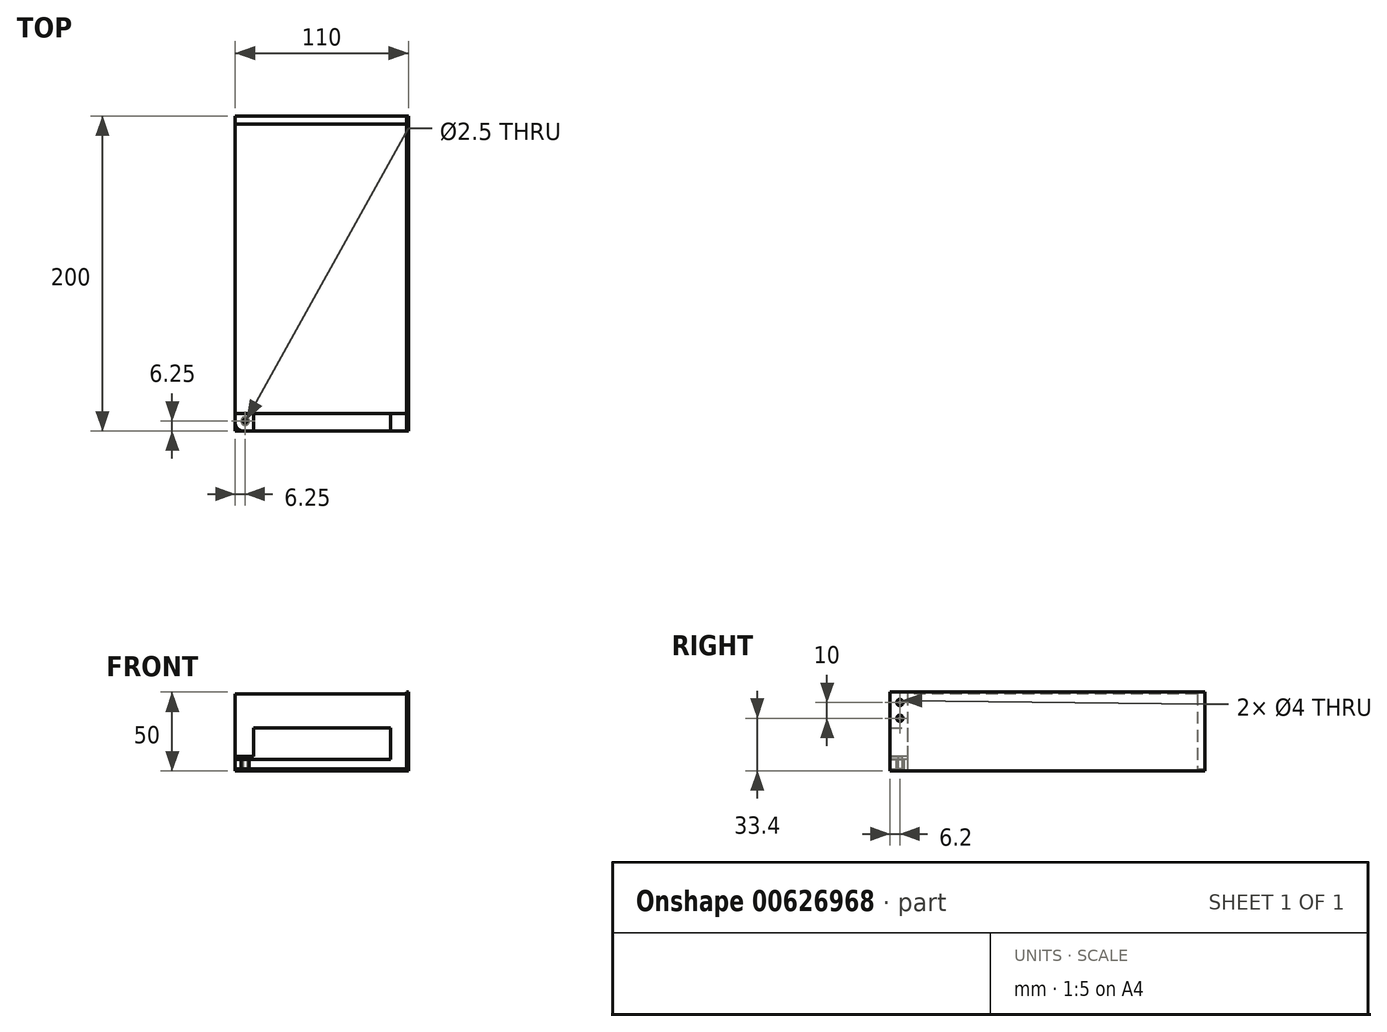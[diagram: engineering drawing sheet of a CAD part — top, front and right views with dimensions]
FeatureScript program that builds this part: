
annotation { "Feature Type Name" : "Feature", "Feature Type Description" : "" }
export const myFeature = defineFeature(function(context is Context, id is Id, definition is map)
    precondition{}
    {
        {
            var Q0;
            Q0=qCreatedBy(makeId("Front.planeOp"),FACE);
            var sketch = newSketch(context, id + "F0", { "sketchPlane" : qUnion([Q0])});
            skLineSegment(sketch, "E0", {"start": v(0, 0) * mm, "end": v(110, 0) * mm});
            skLineSegment(sketch, "E1", {"start": v(110, 0) * mm, "end": v(110, 50) * mm});
            skLineSegment(sketch, "E2", {"start": v(110, 50) * mm, "end": v(108.7, 50) * mm});
            skLineSegment(sketch, "E3", {"start": v(108.7, 50) * mm, "end": v(108.7, 1.3) * mm});
            skLineSegment(sketch, "E4", {"start": v(108.7, 1.3) * mm, "end": v(0, 1.3) * mm});
            skLineSegment(sketch, "E5", {"start": v(0, 1.3) * mm, "end": v(0, 0) * mm});
            skSolve(sketch);
        }
        {
            var Q0;
            Q0=makeQuery(id+"F0.imprint","IMPRINT",FACE,{"disambiguationData":[TD([[makeQuery(id+"F0.imprint","IMPRINT",EDGE,{"derivedFrom":sQuery(id+"F0.wireOp",EDGE,"E0")}),1.0]])]});
            extrude(context, id + "F1", {"entities" : qUnion([Q0]), "depth" : 200 * mm, "offsetDistance" : 25 * mm});
        }
        {
            var Q0;
            Q0=makeQuery(id+"F1.opExtrude","SWEPT_FACE",FACE,{"disambiguationData":[OSD([sQuery(id+"F0.wireOp",EDGE,"E4")])]});
            var sketch = newSketch(context, id + "F2", { "sketchPlane" : qUnion([Q0])});
            skLineSegment(sketch, "E6.0", {"start": v(0, -200) * mm, "end": v(0, 0) * mm});
            skLineSegment(sketch, "E7.0", {"start": v(108.7, -200) * mm, "end": v(108.7, 0) * mm});
            skLineSegment(sketch, "E8", {"start": v(0, -189) * mm, "end": v(108.7, -189) * mm});
            skLineSegment(sketch, "E9", {"start": v(0, -5) * mm, "end": v(108.7, -5) * mm});
            skSolve(sketch);
        }
        {
            var Q0;
            {var subQ0=sQuery(id+"F2.wireOp",EDGE,"E8");Q0=makeQuery(id+"F2.imprint","IMPRINT",FACE,{"disambiguationData":[TD([[makeQuery(id+"F2.imprint","IMPRINT",EDGE,{"derivedFrom":subQ0}),1.0]])]});}
            var Q1;
            Q1=makeQuery(id+"F1.opExtrude","SWEPT_FACE",FACE,{"disambiguationData":[OSD([sQuery(id+"F0.wireOp",EDGE,"E2")])]});
            extrude(context, id + "F3", {"entities" : qUnion([Q0]), "operationType" : NewBodyOperationType.ADD, "endBound" : BoundingType.UP_TO_SURFACE, "depth" : 25 * mm, "endBoundEntityFace" : qUnion([Q1]), "hasOffset" : true, "offsetDistance" : 1 * mm});
        }
        {
            var Q0;
            Q0=makeQuery(id+"F1.opExtrude","SWEPT_FACE",FACE,{"disambiguationData":[OSD([sQuery(id+"F0.wireOp",EDGE,"E1")])]});
            var sketch = newSketch(context, id + "F4", { "sketchPlane" : qUnion([Q0])});
            skCircle(sketch, "E10", {"center": v(-193.8, 43.4) * mm, "radius": 2 * mm});
            skLineSegment(sketch, "E11.0", {"start": v(-189, 49) * mm, "end": v(-189, 1.3) * mm, "construction": true});
            skCircle(sketch, "E12", {"center": v(-193.8, 33.4) * mm, "radius": 2 * mm});
            skSolve(sketch);
        }
        {
            var Q0;
            {var subQ1=sQuery(id+"F0.wireOp",EDGE,"E4");Q0=makeQuery(id+"F3.boolean.opBoolean","SPLIT",FACE,{"disambiguationData":[TD([makeQuery(id+"F3.opExtrude","SWEPT_FACE",FACE,{"disambiguationData":[OSD([sQuery(id+"F2.wireOp",EDGE,"E8")])]})])],"derivedFrom":makeQuery(id+"F1.opExtrude","SWEPT_FACE",FACE,{"disambiguationData":[OSD([subQ1])]})});}
            var sketch = newSketch(context, id + "F5", { "sketchPlane" : qUnion([Q0])});
            skCircle(sketch, "E13", {"center": v(6.25, -193.75) * mm, "radius": 1.25 * mm});
            skCircle(sketch, "E14", {"center": v(6.25, -193.75) * mm, "radius": 2.6 * mm});
            skSolve(sketch);
        }
        {
            var Q0;
            Q0=makeQuery(id+"F5.imprint","IMPRINT",FACE,{"disambiguationData":[TD([[makeQuery(id+"F5.imprint","IMPRINT",EDGE,{"derivedFrom":sQuery(id+"F5.wireOp",EDGE,"E13")}),-1.0]])]});
            extrude(context, id + "F6", {"entities" : qUnion([Q0]), "operationType" : NewBodyOperationType.ADD, "depth" : (8 - 1.9) * mm, "offsetDistance" : 25 * mm});
        }
        {
            var Q0;
            Q0=makeQuery(id+"F6.opExtrude","CAP_FACE",FACE,{"disambiguationData":[OSD([sQuery(id+"F5.wireOp",EDGE,"E13"),sQuery(id+"F5.wireOp",EDGE,"E14")])],"isStart":false});
            var sketch = newSketch(context, id + "F7", { "sketchPlane" : qUnion([Q0])});
            skLineSegment(sketch, "E15.0", {"start": v(108.7, -189) * mm, "end": v(0, -189) * mm});
            skLineSegment(sketch, "E16.0", {"start": v(108.7, -200) * mm, "end": v(108.7, -189) * mm});
            skPoint(sketch, "E17.orphan", {"position": v(108.7, 0) * mm});
            skLineSegment(sketch, "E18", {"start": v(0, -189) * mm, "end": v(0, -195) * mm});
            skLineSegment(sketch, "E19", {"start": v(5, -200) * mm, "end": v(98.7, -200) * mm});
            skLineSegment(sketch, "E20", {"start": v(98.7, -200) * mm, "end": v(98.7, -189) * mm});
            skPoint(sketch, "E21.visualSharp", {"position": v(0, -200) * mm});
            skArc(sketch, "E21.filletArc", {"start": v(0, -195) * mm, "mid": v(1.46, -198.54) * mm, "end": v(5, -200) * mm});
            skSolve(sketch);
        }
        {
            var Q0;
            {var subQ1=sQuery(id+"F7.wireOp",EDGE,"E18");Q0=makeQuery(id+"F7.imprint","IMPRINT",FACE,{"disambiguationData":[TD([[makeQuery(id+"F7.imprint","IMPRINT",EDGE,{"derivedFrom":subQ1}),1.0]])]});}
            var Q1;
            Q1=makeQuery(id+"F7.imprint","IMPRINT",FACE,{"disambiguationData":[TD([[makeQuery(id+"F7.imprint","IMPRINT",EDGE,{"derivedFrom":makeQuery(id+"F6.opExtrude","CAP_EDGE",EDGE,{"disambiguationData":[OSD([sQuery(id+"F5.wireOp",EDGE,"E13")])],"isStart":false})}),-1.0]])]});
            extrude(context, id + "F8", {"entities" : qUnion([Q0, Q1]), "operationType" : NewBodyOperationType.ADD, "depth" : 1.9 * mm, "offsetDistance" : 25 * mm});
        }
        {
            var Q0;
            Q0=makeQuery(id+"F8.opExtrude","CAP_FACE",FACE,{"disambiguationData":[OSD([sQuery(id+"F5.wireOp",EDGE,"E13"),sQuery(id+"F7.wireOp",EDGE,"E15.0"),sQuery(id+"F7.wireOp",EDGE,"E18"),sQuery(id+"F7.wireOp",EDGE,"E19"),sQuery(id+"F7.wireOp",EDGE,"E20"),sQuery(id+"F7.wireOp",EDGE,"E21.filletArc")])],"isStart":false});
            var sketch = newSketch(context, id + "F9", { "sketchPlane" : qUnion([Q0])});
            skLineSegment(sketch, "E22.0", {"start": v(98.7, -200) * mm, "end": v(98.7, -189) * mm});
            skLineSegment(sketch, "E23.0", {"start": v(5, -200) * mm, "end": v(98.7, -200) * mm});
            skLineSegment(sketch, "E24", {"start": v(11.7, -200) * mm, "end": v(11.7, -189) * mm});
            skLineSegment(sketch, "E25", {"start": v(11.7, -189) * mm, "end": v(98.7, -189) * mm});
            skSolve(sketch);
        }
        {
            var Q0;
            {var subQ0=sQuery(id+"F9.wireOp",EDGE,"E22.0");Q0=makeQuery(id+"F9.imprint","IMPRINT",FACE,{"disambiguationData":[TD([[makeQuery(id+"F9.imprint","IMPRINT",EDGE,{"derivedFrom":subQ0}),1.0]])]});}
            extrude(context, id + "F10", {"entities" : qUnion([Q0]), "operationType" : NewBodyOperationType.ADD, "depth" : 18 * mm, "offsetDistance" : 25 * mm});
        }
        {
            var Q0;
            Q0=makeQuery(id+"F4.imprint","IMPRINT",FACE,{"disambiguationData":[TD([[makeQuery(id+"F4.imprint","IMPRINT",EDGE,{"derivedFrom":sQuery(id+"F4.wireOp",EDGE,"E10")}),1.0]])]});
            var Q1;
            Q1=makeQuery(id+"F4.imprint","IMPRINT",FACE,{"disambiguationData":[TD([[makeQuery(id+"F4.imprint","IMPRINT",EDGE,{"derivedFrom":sQuery(id+"F4.wireOp",EDGE,"E12")}),1.0]])]});
            extrude(context, id + "F11", {"entities" : qUnion([Q0, Q1]), "operationType" : NewBodyOperationType.REMOVE, "endBound" : BoundingType.THROUGH_ALL, "oppositeDirection" : true, "depth" : 25 * mm, "offsetDistance" : 25 * mm});
        }
        {
            var Q0;
            {var subQ1=sQuery(id+"F0.wireOp",EDGE,"E4");Q0=makeQuery(id+"F6.boolean.opBoolean","SPLIT",FACE,{"disambiguationData":[TD([makeQuery(id+"F6.opExtrude","SWEPT_FACE",FACE,{"disambiguationData":[OSD([sQuery(id+"F5.wireOp",EDGE,"E13")])]})])],"derivedFrom":makeQuery(id+"F3.boolean.opBoolean","SPLIT",FACE,{"disambiguationData":[TD([makeQuery(id+"F3.opExtrude","SWEPT_FACE",FACE,{"disambiguationData":[OSD([sQuery(id+"F2.wireOp",EDGE,"E8")])]})])],"derivedFrom":makeQuery(id+"F1.opExtrude","SWEPT_FACE",FACE,{"disambiguationData":[OSD([subQ1])]})})});}
            extrude(context, id + "F12", {"entities" : qUnion([Q0]), "operationType" : NewBodyOperationType.REMOVE, "endBound" : BoundingType.THROUGH_ALL, "oppositeDirection" : true, "depth" : 25 * mm, "offsetDistance" : 25 * mm});
        }
    });
